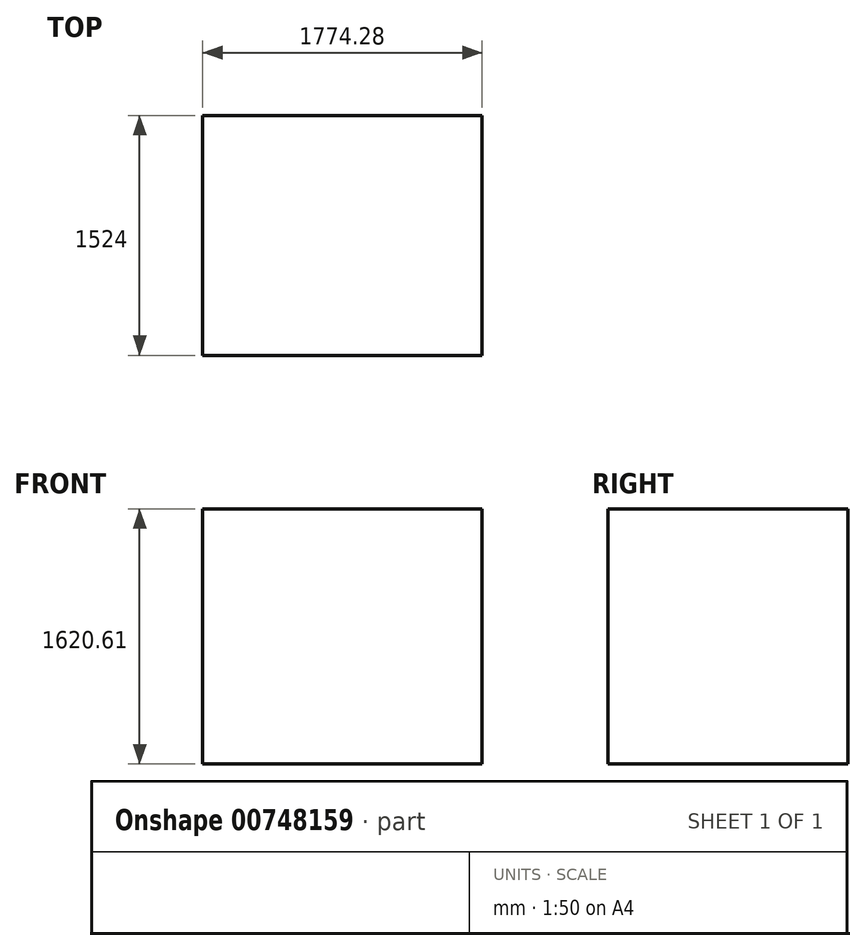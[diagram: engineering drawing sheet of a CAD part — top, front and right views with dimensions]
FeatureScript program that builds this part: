
annotation { "Feature Type Name" : "Feature", "Feature Type Description" : "" }
export const myFeature = defineFeature(function(context is Context, id is Id, definition is map)
    precondition{}
    {
        {
            var Q0;
            Q0=qCreatedBy(makeId("Front.planeOp"),FACE);
            var sketch = newSketch(context, id + "F0", { "sketchPlane" : qUnion([Q0])});
            skLineSegment(sketch, "E0.bottom", {"start": v(0, 0) * mm, "end": v(-7620, 0) * mm});
            skLineSegment(sketch, "E0.top", {"start": v(0, -5080) * mm, "end": v(-7620, -5080) * mm});
            skLineSegment(sketch, "E0.left", {"start": v(0, 0) * mm, "end": v(0, -5080) * mm});
            skLineSegment(sketch, "E0.right", {"start": v(-7620, 0) * mm, "end": v(-7620, -5080) * mm});
            skLineSegment(sketch, "E1.bottom", {"start": v(-4916.66, -1831.95) * mm, "end": v(-3142.38, -1831.95) * mm});
            skLineSegment(sketch, "E1.top", {"start": v(-4916.66, -3452.56) * mm, "end": v(-3142.38, -3452.56) * mm});
            skLineSegment(sketch, "E1.left", {"start": v(-4916.66, -1831.95) * mm, "end": v(-4916.66, -3452.56) * mm});
            skLineSegment(sketch, "E1.right", {"start": v(-3142.38, -1831.95) * mm, "end": v(-3142.38, -3452.56) * mm});
            skSolve(sketch);
        }
        {
            var Q0;
            Q0=makeQuery(id+"F0.imprint","IMPRINT",FACE,{"disambiguationData":[TD([[makeQuery(id+"F0.imprint","IMPRINT",EDGE,{"derivedFrom":sQuery(id+"F0.wireOp",EDGE,"E1.bottom")}),-1.0]])]});
            extrude(context, id + "F1", {"entities" : qUnion([Q0]), "depth" : 1524 * mm, "offsetDistance" : 25.4 * mm});
        }
    });
